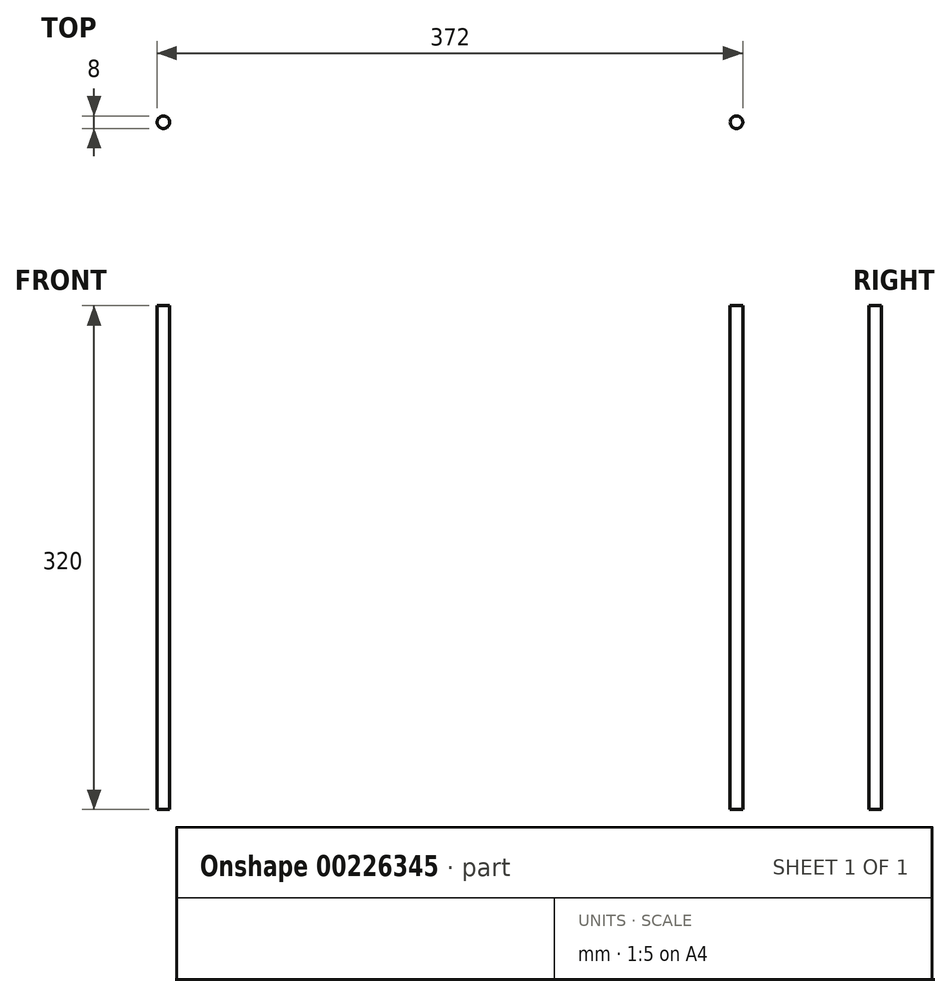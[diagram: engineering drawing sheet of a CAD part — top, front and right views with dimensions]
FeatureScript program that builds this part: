
annotation { "Feature Type Name" : "Feature", "Feature Type Description" : "" }
export const myFeature = defineFeature(function(context is Context, id is Id, definition is map)
    precondition{}
    {
        {
            var Q0;
            Q0=qCreatedBy(makeId("Top.planeOp"),FACE);
            var sketch = newSketch(context, id + "F0", { "sketchPlane" : qUnion([Q0])});
            skCircle(sketch, "E0", {"center": v(0, 0) * mm, "radius": 4 * mm});
            skCircle(sketch, "E1", {"center": v(-364, 0) * mm, "radius": 4 * mm});
            skSolve(sketch);
        }
        {
            var Q0;
            Q0 = qSketchRegion(id + "F0", true);
            extrude(context, id + "F1", {"entities" : qUnion([Q0]), "oppositeDirection" : true, "depth" : 320 * mm});
        }
    });
